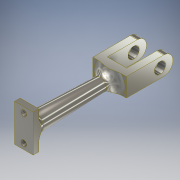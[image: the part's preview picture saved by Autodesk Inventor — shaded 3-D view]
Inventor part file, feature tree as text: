
AUTODESK INVENTOR PART (.ipt)
format: ipt  version: 2017 (Build 210142000, 142)  size: 248,832 bytes
history: native  units: mm
features: sketch x8, extrude x6, fillet x3, plane x2, loft x1, mirror x1
ambient origin geometry x8: Origin, YZ Plane, XZ Plane, XY Plane, X Axis, Y Axis, Z Axis, Center Point
bodies: Solid1 (feature_tree)
feature tree (21):
  sketch  "Sketch1"  dims[d0=9.5mm d1=43.0mm d2=6.5mm]
  plane  "Work Plane1"
  loft  "Loft1"
  extrude  "Extrusion1"  TaperAngle=0.0deg  [1 undecoded]
  extrude  "Extrusion2"  Depth=3.0mm TaperAngle=0.0deg
  extrude  "Extrusion3"  Depth=3.0mm
  fillet  "Fillet1"  [1 undecoded]
  extrude  "Extrusion5"  Depth=5.0mm
  fillet  "Fillet4"  Radius=5.0mm
  extrude  "Extrusion8"  Depth=5.0mm
  fillet  "Fillet5"  [1 undecoded]
  extrude  "Extrusion9"  TaperAngle=0.0deg  [1 undecoded]
  plane  "Work Plane2"
  mirror  "Mirror1"
  sketch  "Sketch2"  dims[d3=0.0mm d4=90.0deg d5=0.0mm d6=90.0deg]
  sketch  "Sketch3"  dims[d7=5.0mm d8=10.0mm d9=10.0mm d10=20.0mm d11=10.0mm d12=3.0mm d13=0.0mm]
  sketch  "Sketch4"  dims[d14=10.0mm d15=3.0mm d16=0.0mm]
  sketch  "Sketch5"  dims[d17=3.0mm d18=14.0mm d19=3.0mm d20=3.0mm d21=5.0mm d22=0.0mm d29=3.0mm d31=0.0mm]
  sketch  "Sketch7"  dims[d32=0.0mm d33=9.5mm d34=5.0mm]
  sketch  "Sketch10"  dims[d35=0.0mm d36=5.0mm d37=0.0mm]
  sketch  "Sketch11"  dims[d38=0.0mm d39=0.0mm d40=10.0mm d41=5.0mm d42=0.0mm d43=10.0mm d61=4.0mm d62=0.0mm d71=5.0mm d79=10.0mm d80=4.5mm d81=10.0mm d82=14.0mm d83=18.0mm d84=9.0mm d85=4.0mm d86=9.0mm d87=9.0mm d89=21.0mm d90=0.0mm d91=5.0mm d92=6.0mm d93=5.0mm d94=5.361925mm d95=21.0mm d96=0.0mm d97=0.0mm]
note: 4 required parameter values undecoded (feature->parameter linkage not recoverable at this tier; creation-order binding heuristic only, values carry confidence <= 0.55)
